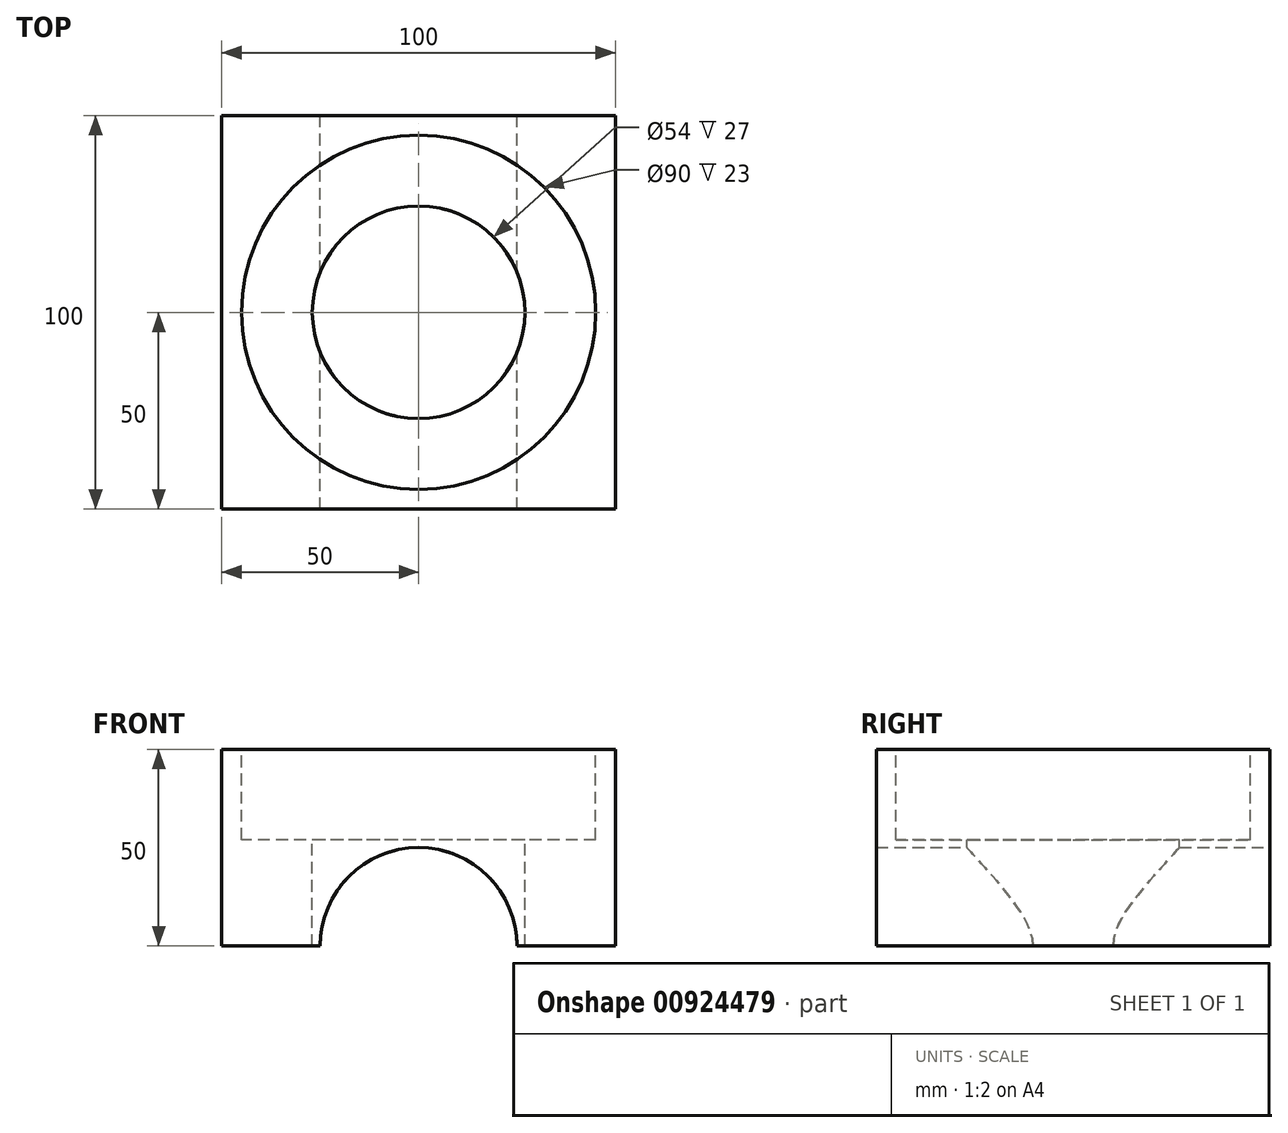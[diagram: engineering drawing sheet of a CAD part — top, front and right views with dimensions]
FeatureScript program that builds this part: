
annotation { "Feature Type Name" : "Feature", "Feature Type Description" : "" }
export const myFeature = defineFeature(function(context is Context, id is Id, definition is map)
    precondition{}
    {
        {
            var Q0;
            Q0=qCreatedBy(makeId("Front.planeOp"),FACE);
            var sketch = newSketch(context, id + "F0", { "sketchPlane" : qUnion([Q0])});
            skCircle(sketch, "E0", {"center": v(0, 0) * mm, "radius": 25 * mm});
            skLineSegment(sketch, "E1", {"start": v(0, 0) * mm, "end": v(0, 25) * mm});
            skLineSegment(sketch, "E2.bottom", {"start": v(50, 0) * mm, "end": v(-50, 0) * mm});
            skLineSegment(sketch, "E2.top", {"start": v(50, 50) * mm, "end": v(-50, 50) * mm});
            skLineSegment(sketch, "E2.left", {"start": v(50, 0) * mm, "end": v(50, 50) * mm});
            skLineSegment(sketch, "E2.right", {"start": v(-50, 0) * mm, "end": v(-50, 50) * mm});
            skPoint(sketch, "E2.middle", {"position": v(0, 25) * mm});
            skSolve(sketch);
        }
        {
            var Q0;
            {var subQ1=sQuery(id+"F0.wireOp",EDGE,"E2.top");Q0=makeQuery(id+"F0.imprint","IMPRINT",FACE,{"disambiguationData":[TD([[makeQuery(id+"F0.imprint","IMPRINT",EDGE,{"derivedFrom":subQ1}),1.0]])]});}
            extrude(context, id + "F1", {"entities" : qUnion([Q0]), "depth" : 100 * mm, "offsetDistance" : 25 * mm, "symmetric" : true});
        }
        {
            var Q0;
            Q0=makeQuery(id+"F1.opExtrude","SWEPT_FACE",FACE,{"disambiguationData":[OSD([sQuery(id+"F0.wireOp",EDGE,"E2.top")])]});
            var sketch = newSketch(context, id + "F2", { "sketchPlane" : qUnion([Q0])});
            skCircle(sketch, "E3", {"center": v(0, 0) * mm, "radius": 27 * mm});
            skSolve(sketch);
        }
        {
            var Q0;
            Q0=qSketchRegion(id+"F2",true);
            extrude(context, id + "F3", {"entities" : qUnion([Q0]), "operationType" : NewBodyOperationType.REMOVE, "oppositeDirection" : true, "depth" : 50 * mm, "offsetDistance" : 25 * mm});
        }
        {
            var Q0;
            Q0=makeQuery(id+"F1.opExtrude","SWEPT_FACE",FACE,{"disambiguationData":[OSD([sQuery(id+"F0.wireOp",EDGE,"E2.top")])]});
            var sketch = newSketch(context, id + "F4", { "sketchPlane" : qUnion([Q0])});
            skCircle(sketch, "E4", {"center": v(0, 0) * mm, "radius": 45 * mm});
            skSolve(sketch);
        }
        {
            var Q0;
            Q0=qSketchRegion(id+"F4",true);
            extrude(context, id + "F5", {"entities" : qUnion([Q0]), "operationType" : NewBodyOperationType.REMOVE, "oppositeDirection" : true, "depth" : 23 * mm, "offsetDistance" : 25 * mm});
        }
    });
